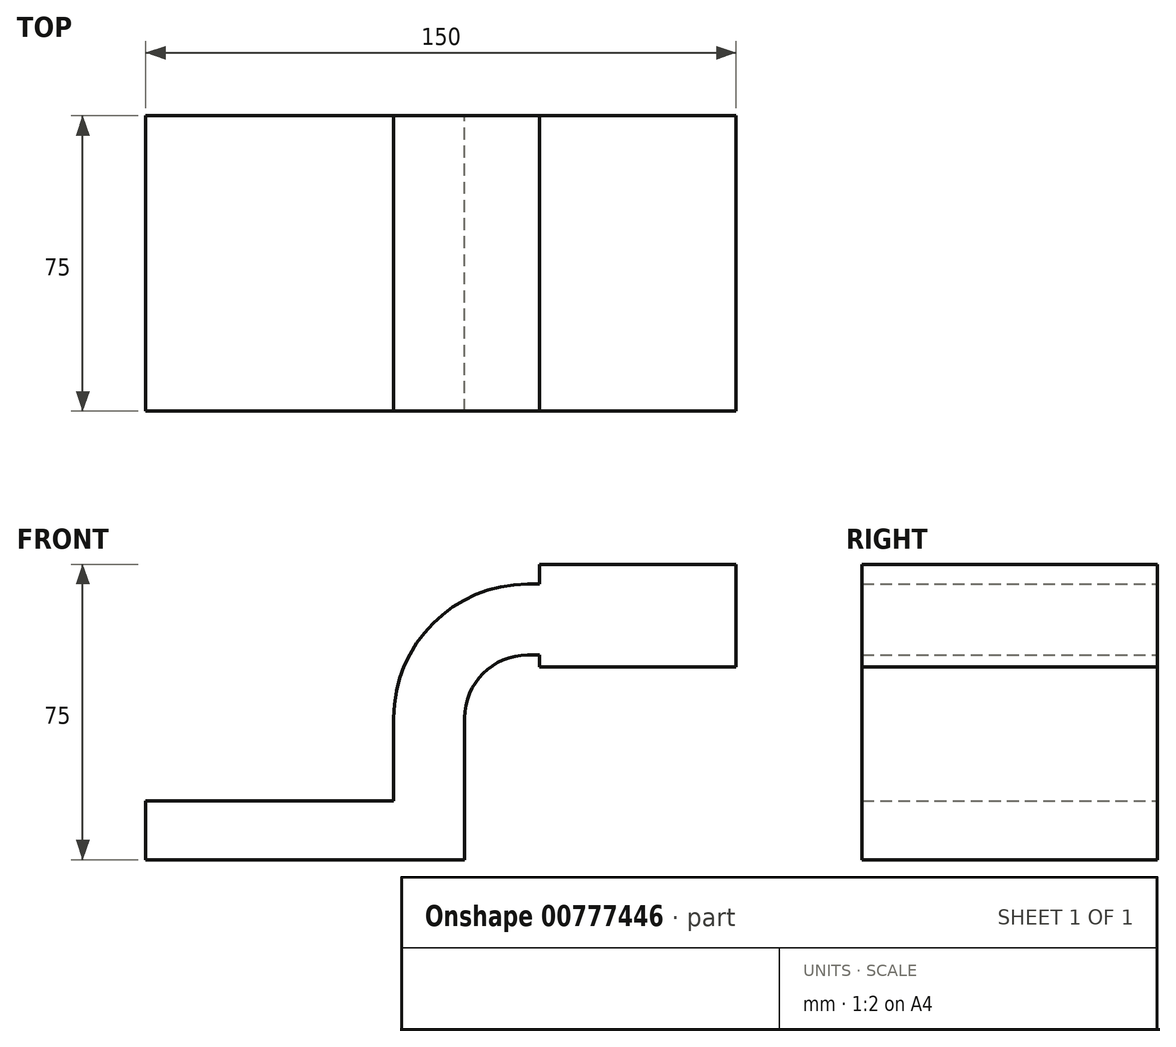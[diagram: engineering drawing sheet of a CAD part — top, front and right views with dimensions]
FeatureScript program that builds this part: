
annotation { "Feature Type Name" : "Feature", "Feature Type Description" : "" }
export const myFeature = defineFeature(function(context is Context, id is Id, definition is map)
    precondition{}
    {
        {
            var Q0;
            Q0=qCreatedBy(makeId("Front.planeOp"),FACE);
            var sketch = newSketch(context, id + "F0", { "sketchPlane" : qUnion([Q0])});
            skLineSegment(sketch, "E0.bottom", {"start": v(40.5, 7.5) * mm, "end": v(-40.5, 7.5) * mm});
            skLineSegment(sketch, "E0.top", {"start": v(40.5, -7.5) * mm, "end": v(-40.5, -7.5) * mm});
            skLineSegment(sketch, "E0.left", {"start": v(40.5, 7.5) * mm, "end": v(40.5, -7.5) * mm});
            skLineSegment(sketch, "E0.right", {"start": v(-40.5, 7.5) * mm, "end": v(-40.5, -7.5) * mm});
            skPoint(sketch, "E0.middle", {"position": v(0, 0) * mm});
            skLineSegment(sketch, "E1.bottom", {"start": v(109.5, 67.5) * mm, "end": v(59.5, 67.5) * mm});
            skLineSegment(sketch, "E1.top", {"start": v(109.5, 41.5) * mm, "end": v(59.5, 41.5) * mm});
            skLineSegment(sketch, "E1.left", {"start": v(109.5, 67.5) * mm, "end": v(109.5, 41.5) * mm});
            skLineSegment(sketch, "E1.right", {"start": v(59.5, 67.5) * mm, "end": v(59.5, 41.5) * mm});
            skPoint(sketch, "E1.middle", {"position": v(84.5, 54.5) * mm});
            skArc(sketch, "E2", {"start": v(40.5, 28.5) * mm, "mid": v(45.19, 39.81) * mm, "end": v(56.5, 44.5) * mm});
            skLineSegment(sketch, "E3", {"start": v(56.5, 44.5) * mm, "end": v(84.5, 44.5) * mm});
            skLineSegment(sketch, "E4", {"start": v(40.5, 7.5) * mm, "end": v(40.5, 28.5) * mm});
            skLineSegment(sketch, "E5.0", {"start": v(56.5, 62.5) * mm, "end": v(84.5, 62.5) * mm});
            skArc(sketch, "E5.1", {"start": v(22.5, 28.5) * mm, "mid": v(32.46, 52.54) * mm, "end": v(56.5, 62.5) * mm});
            skLineSegment(sketch, "E5.2", {"start": v(22.5, 7.5) * mm, "end": v(22.5, 28.5) * mm});
            skLineSegment(sketch, "E6", {"start": v(84.5, 41.5) * mm, "end": v(84.5, 67.5) * mm});
            skFitSpline(sketch, "E7", {"points": [v(-40.5, 7.5) * mm, v(56.5, 62.5) * mm], "startDerivative": vector(-5.74, 113.45) * mm, "endDerivative": vector(125.04, -1.58) * mm});
            skSolve(sketch);
        }
        {
            var Q0;
            Q0=makeQuery(id+"F0.imprint","IMPRINT",FACE,{"disambiguationData":[TD([[makeQuery(id+"F0.imprint","IMPRINT",EDGE,{"derivedFrom":sQuery(id+"F0.wireOp",EDGE,"E5.1")}),1.0]])]});
            var Q1;
            {var subQ1=sQuery(id+"F0.wireOp",EDGE,"E2");Q1=makeQuery(id+"F0.imprint","IMPRINT",FACE,{"disambiguationData":[TD([[makeQuery(id+"F0.imprint","IMPRINT",EDGE,{"derivedFrom":subQ1}),1.0]])]});}
            var Q2;
            {var subQ0=sQuery(id+"F0.wireOp",EDGE,"E1.right");var subQ1=sQuery(id+"F0.wireOp",EDGE,"E1.bottom");var subQ2=makeQuery(id+"F0.imprint","INTERSECT",VERTEX,{"derivedFrom":[subQ1,subQ0]});Q2=makeQuery(id+"F0.imprint","IMPRINT",FACE,{"disambiguationData":[TD([[makeQuery(id+"F0.imprint","IMPRINT",EDGE,{"disambiguationData":[TD([[subQ2,1.0]])],"derivedFrom":subQ1}),1.0]])]});}
            var Q3;
            {var subQ0=sQuery(id+"F0.wireOp",EDGE,"E5.0");var subQ1=sQuery(id+"F0.wireOp",EDGE,"E1.right");var subQ2=makeQuery(id+"F0.imprint","INTERSECT",VERTEX,{"derivedFrom":[subQ1,subQ0]});Q3=makeQuery(id+"F0.imprint","IMPRINT",FACE,{"disambiguationData":[TD([[makeQuery(id+"F0.imprint","IMPRINT",EDGE,{"disambiguationData":[TD([[subQ2,-1.0]])],"derivedFrom":subQ1}),1.0]])]});}
            var Q4;
            {var subQ0=sQuery(id+"F0.wireOp",EDGE,"E1.right");var subQ1=sQuery(id+"F0.wireOp",EDGE,"E1.top");var subQ2=makeQuery(id+"F0.imprint","INTERSECT",VERTEX,{"derivedFrom":[subQ1,subQ0]});Q4=makeQuery(id+"F0.imprint","IMPRINT",FACE,{"disambiguationData":[TD([[makeQuery(id+"F0.imprint","IMPRINT",EDGE,{"disambiguationData":[TD([[subQ2,1.0]])],"derivedFrom":subQ1}),-1.0]])]});}
            var Q5;
            {var subQ4=sQuery(id+"F0.wireOp",EDGE,"E1.left");Q5=makeQuery(id+"F0.imprint","IMPRINT",FACE,{"disambiguationData":[TD([[makeQuery(id+"F0.imprint","IMPRINT",EDGE,{"derivedFrom":subQ4}),-1.0]])]});}
            var Q6;
            Q6=makeQuery(id+"F0.imprint","IMPRINT",FACE,{"disambiguationData":[TD([[makeQuery(id+"F0.imprint","IMPRINT",EDGE,{"derivedFrom":sQuery(id+"F0.wireOp",EDGE,"E0.top")}),-1.0]])]});
            extrude(context, id + "F1", {"entities" : qUnion([Q0, Q1, Q2, Q3, Q4, Q5, Q6]), "endBound" : BoundingType.SYMMETRIC, "depth" : 75 * mm, "offsetDistance" : 25 * mm});
        }
    });
